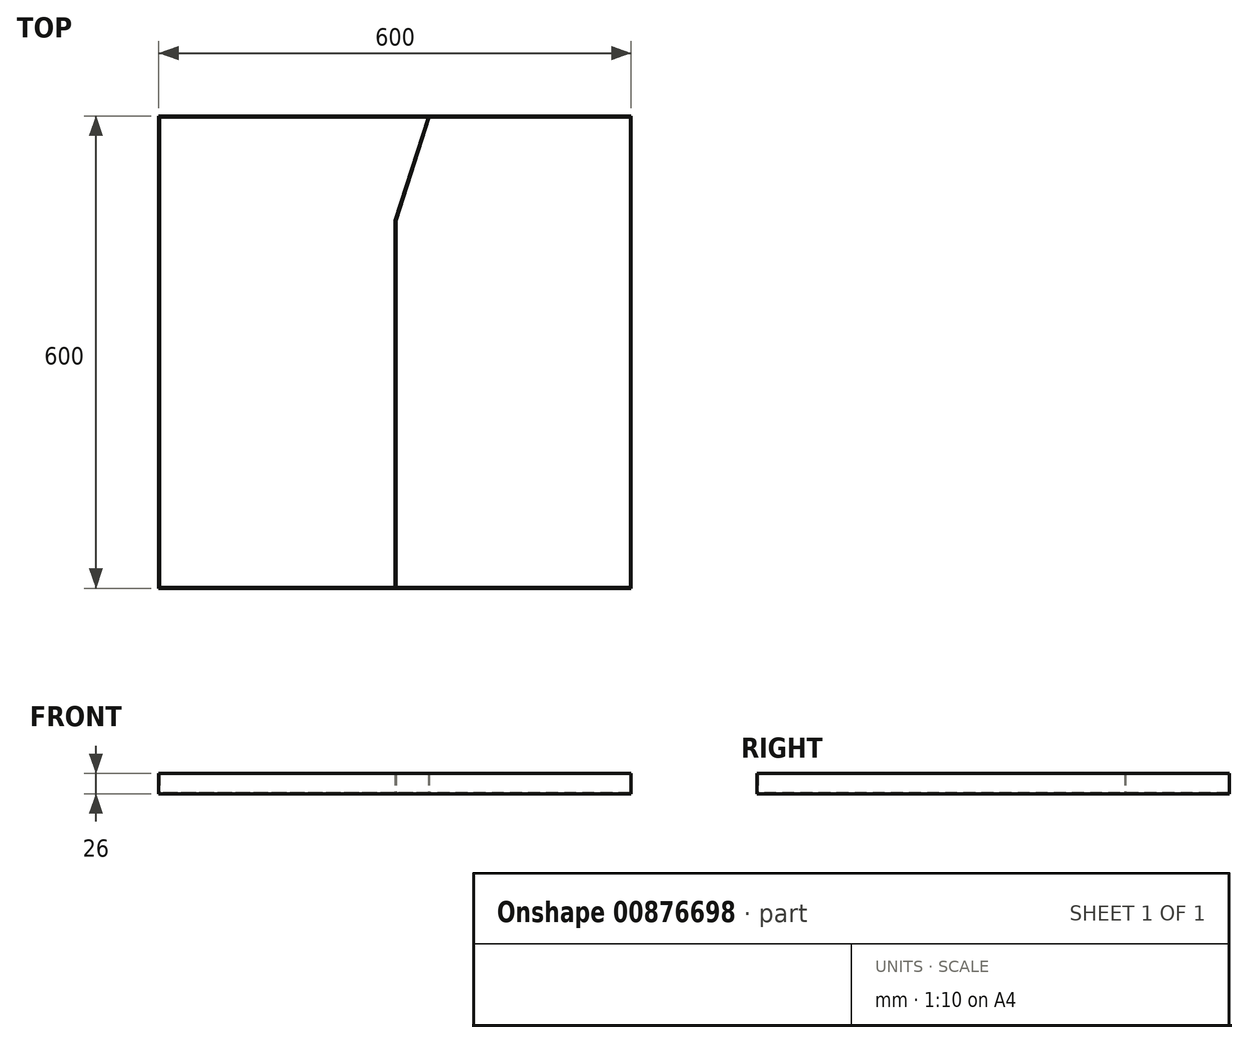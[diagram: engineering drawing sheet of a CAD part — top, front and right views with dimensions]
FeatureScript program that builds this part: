
annotation { "Feature Type Name" : "Feature", "Feature Type Description" : "" }
export const myFeature = defineFeature(function(context is Context, id is Id, definition is map)
    precondition{}
    {
        {
            var Q0;
            Q0=qCreatedBy(makeId("Top.planeOp"),FACE);
            var sketch = newSketch(context, id + "F0", { "sketchPlane" : qUnion([Q0])});
            skLineSegment(sketch, "E0.bottom", {"start": v(300, 300) * mm, "end": v(-300, 300) * mm});
            skLineSegment(sketch, "E0.top", {"start": v(300, -300) * mm, "end": v(-300, -300) * mm});
            skLineSegment(sketch, "E0.left", {"start": v(300, 300) * mm, "end": v(300, -300) * mm});
            skLineSegment(sketch, "E0.right", {"start": v(-300, 300) * mm, "end": v(-300, -300) * mm});
            skPoint(sketch, "E0.middle", {"position": v(0, 0) * mm});
            skSolve(sketch);
        }
        {
            var Q0;
            Q0 = qSketchRegion(id + "F0", true);
            extrude(context, id + "F1", {"entities" : qUnion([Q0]), "depth" : 1 * mm, "offsetDistance" : 25 * mm});
        }
        {
            var Q0;
            Q0=makeQuery(id+"F1.opExtrude","CAP_FACE",FACE,{"disambiguationData":[OSD([sQuery(id+"F0.wireOp",EDGE,"E0.bottom"),sQuery(id+"F0.wireOp",EDGE,"E0.top"),sQuery(id+"F0.wireOp",EDGE,"E0.left"),sQuery(id+"F0.wireOp",EDGE,"E0.right")])],"isStart":false});
            var sketch = newSketch(context, id + "F2", { "sketchPlane" : qUnion([Q0])});
            skLineSegment(sketch, "E1.0", {"start": v(299, 299) * mm, "end": v(43.43, 299) * mm});
            skLineSegment(sketch, "E1.1", {"start": v(299, 299) * mm, "end": v(299, -299) * mm});
            skLineSegment(sketch, "E1.2", {"start": v(299, -299) * mm, "end": v(1, -299) * mm});
            skLineSegment(sketch, "E1.3", {"start": v(-299, 299) * mm, "end": v(-299, -299) * mm});
            skLineSegment(sketch, "E2.bottom", {"start": v(-300, 300) * mm, "end": v(300, 300) * mm});
            skLineSegment(sketch, "E2.top", {"start": v(-300, -300) * mm, "end": v(300, -300) * mm});
            skLineSegment(sketch, "E2.left", {"start": v(-300, 300) * mm, "end": v(-300, -300) * mm});
            skLineSegment(sketch, "E2.right", {"start": v(300, 300) * mm, "end": v(300, -300) * mm});
            skLineSegment(sketch, "E3", {"start": v(0, -299) * mm, "end": v(0, 167.51) * mm});
            skLineSegment(sketch, "E4", {"start": v(0, 167.51) * mm, "end": v(42.38, 299) * mm});
            skLineSegment(sketch, "E5.0", {"start": v(1, 167.35) * mm, "end": v(43.43, 299) * mm});
            skLineSegment(sketch, "E5.1", {"start": v(1, -299) * mm, "end": v(1, 167.35) * mm});
            skLineSegment(sketch, "E6.trimOffspring", {"start": v(0, -299) * mm, "end": v(-299, -299) * mm});
            skLineSegment(sketch, "E7.trimOffspring", {"start": v(42.38, 299) * mm, "end": v(-299, 299) * mm});
            skSolve(sketch);
        }
        {
            var Q0;
            Q0 = qSketchRegion(id + "F2", true);
            extrude(context, id + "F3", {"entities" : qUnion([Q0]), "operationType" : NewBodyOperationType.ADD, "depth" : 25 * mm, "offsetDistance" : 25 * mm});
        }
    });
